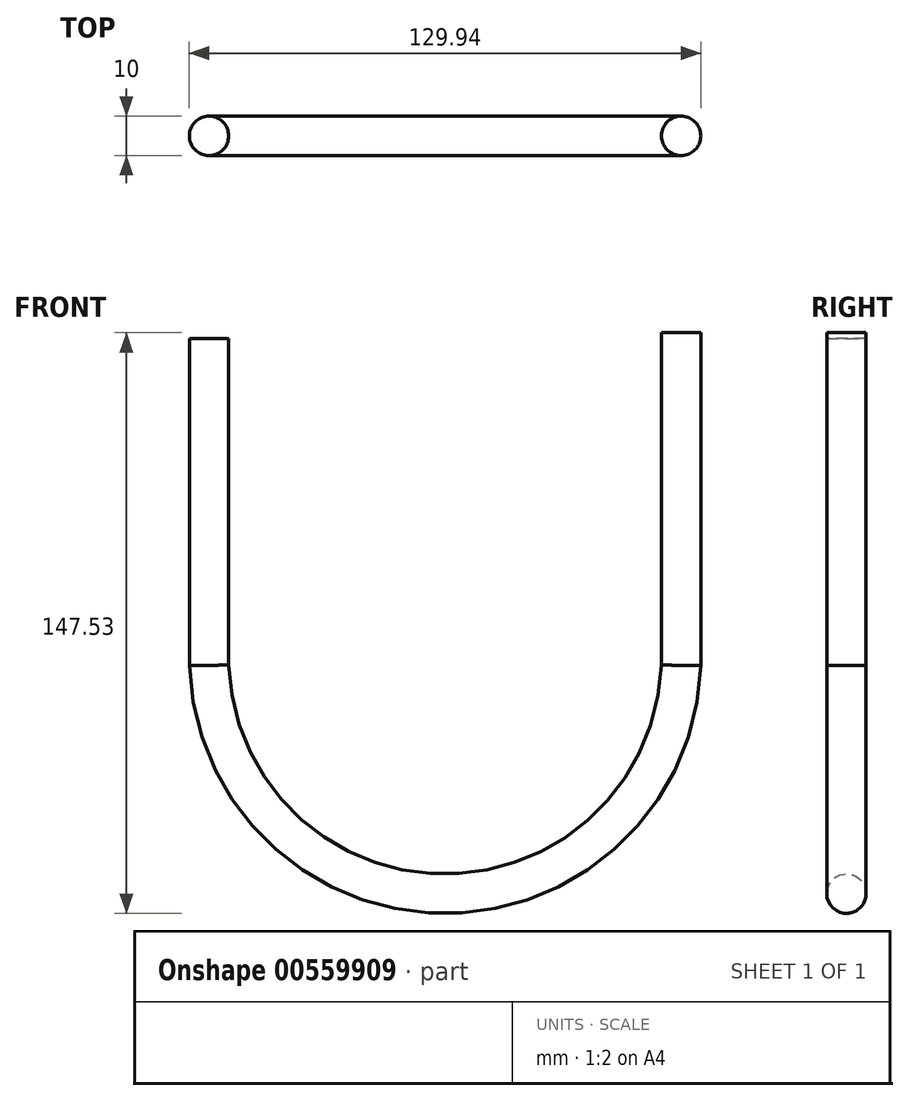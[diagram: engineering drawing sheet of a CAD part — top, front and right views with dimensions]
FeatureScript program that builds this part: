
annotation { "Feature Type Name" : "Feature", "Feature Type Description" : "" }
export const myFeature = defineFeature(function(context is Context, id is Id, definition is map)
    precondition{}
    {
        {
            var Q0;
            Q0=qCreatedBy(makeId("Front.planeOp"),FACE);
            var sketch = newSketch(context, id + "F0", { "sketchPlane" : qUnion([Q0])});
            skLineSegment(sketch, "E0.left", {"start": v(-59.97, 56) * mm, "end": v(-59.97, -27) * mm});
            skLineSegment(sketch, "E0.right", {"start": v(59.97, 57.53) * mm, "end": v(59.97, -27) * mm});
            skPoint(sketch, "E0.middle", {"position": v(0, 0) * mm});
            skArc(sketch, "E1", {"start": v(-59.97, -27) * mm, "mid": v(0, -85) * mm, "end": v(59.97, -27) * mm});
            skPoint(sketch, "E2.orphan", {"position": v(-59.97, -57.53) * mm});
            skPoint(sketch, "E3.orphan", {"position": v(59.97, -56) * mm});
            skSolve(sketch);
        }
        {
            var Q0;
            Q0=sQuery(id+"F0.wireOp",VERTEX,"E0.left.start");
            var Q1;
            Q1=sQuery(id+"F0.wireOp",EDGE,"E0.left");
            cPlane(context, id + "F1", {"entities" : qUnion([Q0, Q1]), "cplaneType" : CPlaneType.LINE_POINT, "offset" : 25 * mm, "width" : 150 * mm, "height" : 150 * mm});
        }
        {
            var Q0;
            Q0=qCreatedBy(id+"F1.planeOp",FACE);
            var sketch = newSketch(context, id + "F2", { "sketchPlane" : qUnion([Q0])});
            skPoint(sketch, "E4.0", {"position": v(-59.97, 0) * mm});
            skCircle(sketch, "E5", {"center": v(-59.97, 0) * mm, "radius": 5 * mm});
            skSolve(sketch);
        }
        {
            var Q0;
            Q0=makeQuery(id+"F2.imprint","IMPRINT",FACE,{"disambiguationData":[TD([[makeQuery(id+"F2.imprint","IMPRINT",EDGE,{"derivedFrom":sQuery(id+"F2.wireOp",EDGE,"E5")}),1.0]])]});
            var Q1;
            Q1=sQuery(id+"F0.wireOp",EDGE,"E0.left");
            var Q2;
            Q2=sQuery(id+"F0.wireOp",EDGE,"E1");
            var Q3;
            Q3=sQuery(id+"F0.wireOp",EDGE,"E0.right");
            sweep(context, id + "F3", {"profiles" : qUnion([Q0]), "path" : qUnion([Q1, Q2, Q3])});
        }
    });
